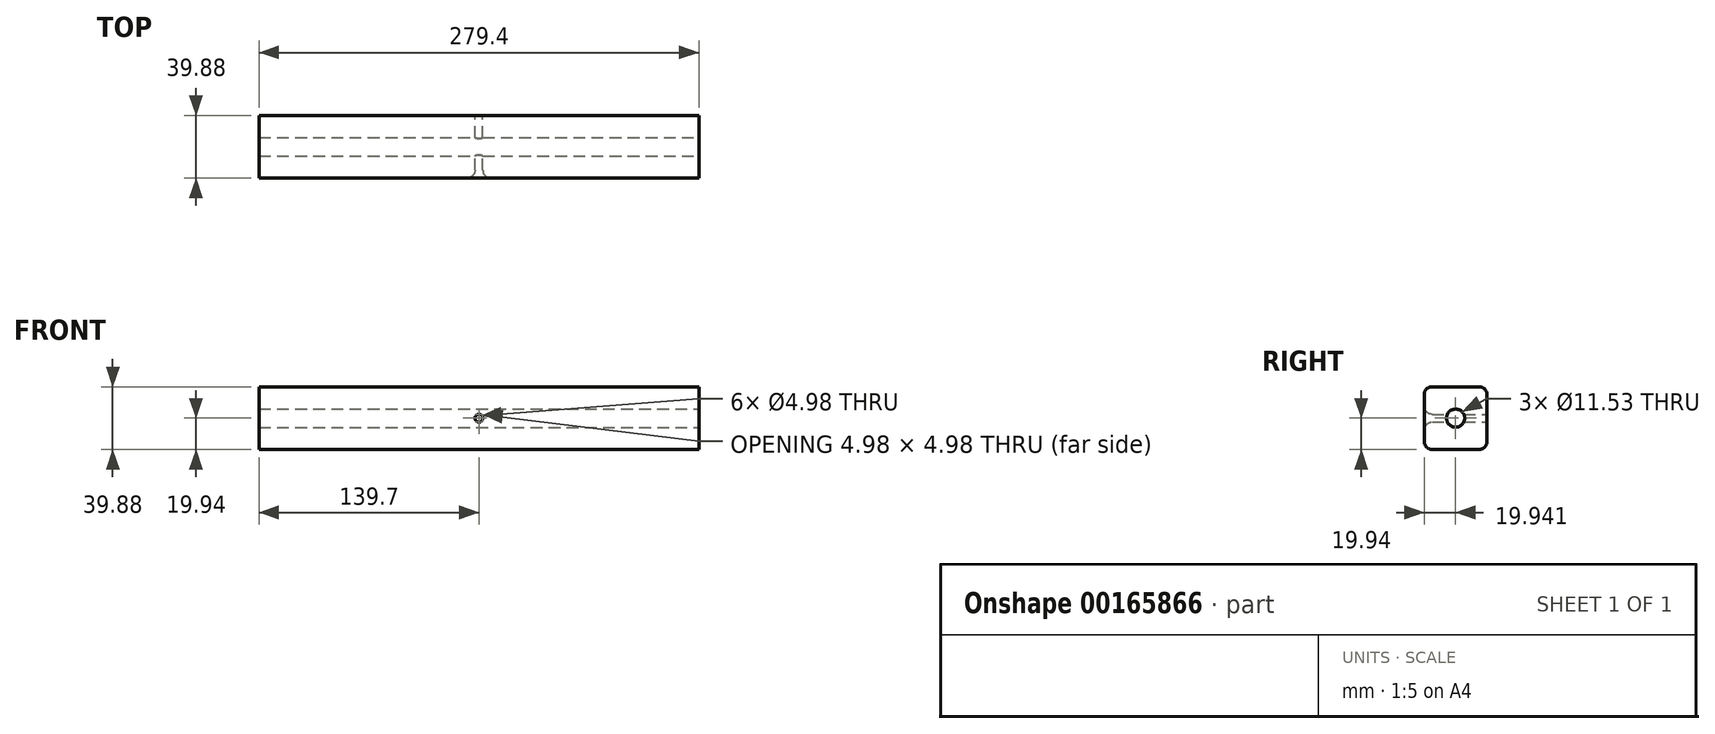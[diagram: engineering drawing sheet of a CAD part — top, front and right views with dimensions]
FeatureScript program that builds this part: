
annotation { "Feature Type Name" : "Feature", "Feature Type Description" : "" }
export const myFeature = defineFeature(function(context is Context, id is Id, definition is map)
    precondition{}
    {
        {
            var Q0;
            Q0=qCreatedBy(makeId("Front.planeOp"),FACE);
            var sketch = newSketch(context, id + "F0", { "sketchPlane" : qUnion([Q0])});
            skLineSegment(sketch, "E0.bottom", {"start": v(139.7, 19.94) * mm, "end": v(-139.7, 19.94) * mm});
            skLineSegment(sketch, "E0.top", {"start": v(139.7, -19.94) * mm, "end": v(-139.7, -19.94) * mm});
            skLineSegment(sketch, "E0.left", {"start": v(139.7, 19.94) * mm, "end": v(139.7, -19.94) * mm});
            skLineSegment(sketch, "E0.right", {"start": v(-139.7, 19.94) * mm, "end": v(-139.7, -19.94) * mm});
            skPoint(sketch, "E0.middle", {"position": v(0, 0) * mm});
            skCircle(sketch, "E1", {"center": v(0, 0) * mm, "radius": 2.49 * mm});
            skLineSegment(sketch, "E2", {"start": v(0, 0) * mm, "end": v(-139.7, 0) * mm});
            skLineSegment(sketch, "E3", {"start": v(0, 0) * mm, "end": v(139.7, 0) * mm});
            skSolve(sketch);
        }
        {
            var Q0;
            Q0 = qSketchRegion(id + "F0", true);
            extrude(context, id + "F1", {"entities" : qUnion([Q0]), "depth" : 39.88 * mm});
        }
        {
            var Q0;
            Q0=makeQuery(id+"F1.opExtrude","SWEPT_FACE",FACE,{"disambiguationData":[OSD([sQuery(id+"F0.wireOp",EDGE,"E0.left")])]});
            var sketch = newSketch(context, id + "F2", { "sketchPlane" : qUnion([Q0])});
            skPoint(sketch, "E4.startSnap0", {"position": v(-39.88, 0) * mm});
            skPoint(sketch, "E4.startSnap1", {"position": v(-19.94, 19.94) * mm});
            skCircle(sketch, "E5", {"center": v(-19.94, 0) * mm, "radius": 5.77 * mm});
            skSolve(sketch);
        }
        {
            var Q0;
            Q0=makeQuery(id+"F2.imprint","IMPRINT",FACE,{"disambiguationData":[TD([[makeQuery(id+"F2.imprint","IMPRINT",EDGE,{"derivedFrom":sQuery(id+"F2.wireOp",EDGE,"E5")}),1.0]])]});
            extrude(context, id + "F3", {"entities" : qUnion([Q0]), "operationType" : NewBodyOperationType.REMOVE, "endBound" : BoundingType.THROUGH_ALL, "oppositeDirection" : true, "depth" : 25.4 * mm});
        }
        {
            var Q0;
            Q0=makeQuery(id+"F3.boolean.opBoolean","COPY",EDGE,{"derivedFrom":makeQuery(id+"F3.opExtrude","CAP_EDGE",EDGE,{"disambiguationData":[OSD([sQuery(id+"F2.wireOp",EDGE,"E5")])],"isStart":true})});
            var Q1;
            Q1=makeQuery(id+"F1.opExtrude","CAP_EDGE",EDGE,{"disambiguationData":[OSD([sQuery(id+"F0.wireOp",EDGE,"E1")])],"isStart":false});
            var Q2;
            Q2=makeQuery(id+"F1.opExtrude","CAP_EDGE",EDGE,{"disambiguationData":[OSD([sQuery(id+"F0.wireOp",EDGE,"E0.bottom")])],"isStart":false});
            var Q3;
            Q3=makeQuery(id+"F1.opExtrude","CAP_EDGE",EDGE,{"disambiguationData":[OSD([sQuery(id+"F0.wireOp",EDGE,"E0.bottom")])],"isStart":true});
            var Q4;
            Q4=makeQuery(id+"F1.opExtrude","CAP_EDGE",EDGE,{"disambiguationData":[OSD([sQuery(id+"F0.wireOp",EDGE,"E0.top")])],"isStart":true});
            var Q5;
            Q5=makeQuery(id+"F1.opExtrude","CAP_EDGE",EDGE,{"disambiguationData":[OSD([sQuery(id+"F0.wireOp",EDGE,"E0.top")])],"isStart":false});
            fillet(context, id + "F4", {"entities" : qUnion([Q0, Q1, Q2, Q3, Q4, Q5]), "radius" : 5.08 * mm, "tangentPropagation" : true, "allowEdgeOverflow" : false});
        }
    });
